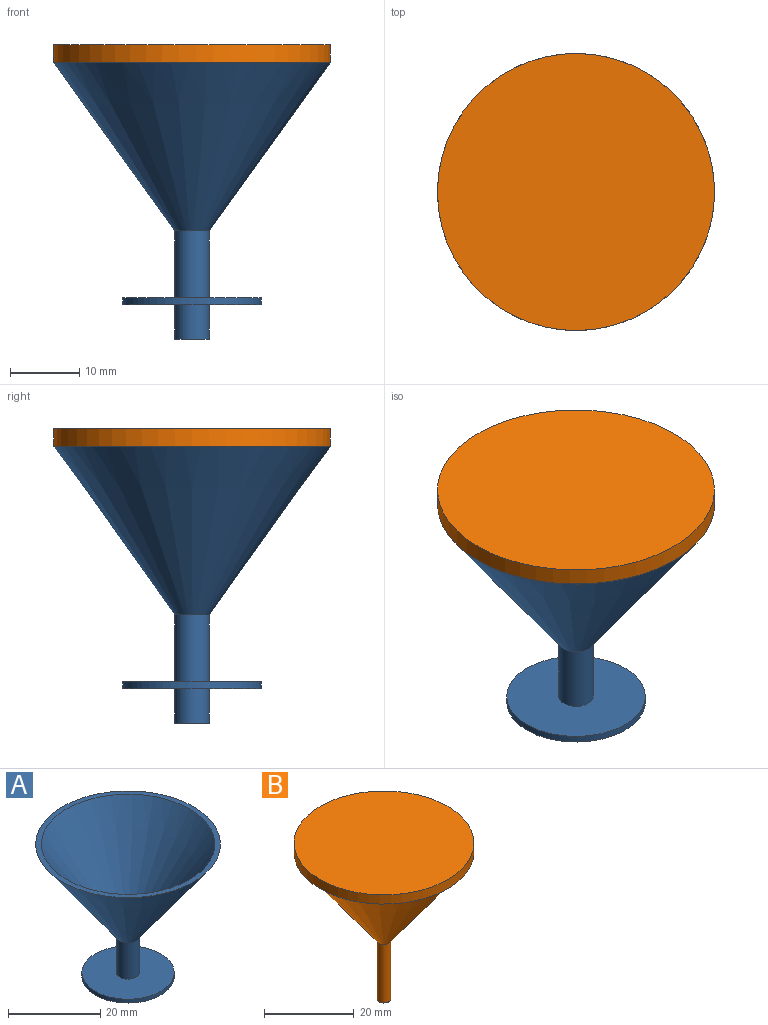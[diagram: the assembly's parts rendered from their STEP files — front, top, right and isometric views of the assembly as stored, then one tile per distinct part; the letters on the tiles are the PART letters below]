
ASSEMBLY  parts=2 mates=1
PART A: 10 faces, bbox 40x40x40 mm
  f0: cone r=18.77mm half-angle=35.7deg, axis (0,0,1), area 1885.1mm2, adj f1,f9
  f1: plane 40x40mm, normal (0,0,1), area 150mm2, adj f0,f2
  f2: cone r=20mm half-angle=35.7deg, axis (0,0,1), area 2120.6mm2, adj f1,f3
  f3: cylinder r=2.5mm len=9.63mm, axis (0,0,1), area 151.3mm2, adj f2,f4
  f4: plane 20x20mm, normal (0,0,1), area 294.5mm2, adj f3,f5
  f5: cylinder r=10mm len=20mm, axis (0,0,1), area 62.8mm2, adj f4,f6
  f6: plane 20x20mm, normal (0,0,-1), area 294.5mm2, adj f5,f7
  f7: cylinder r=2.5mm len=5mm, axis (0,0,1), area 78.5mm2, adj f6,f8
  f8: plane 5x5mm, normal (0,0,-1), area 12.6mm2, adj f7,f9
  f9: cylinder r=1.5mm len=15.96mm, axis (0,0,1), area 150.4mm2, adj f0,f8
PART B: 6 faces, bbox 40x40x42.5 mm
  f0: cylinder r=1.5mm len=15.96mm, axis (0,0,-1), area 150.4mm2, adj f1,f5
  f1: sphere r=1.5mm, area 14.1mm2, adj f0
  f2: plane 40x40mm, normal (0,0,1), area 1256.6mm2, adj f3
  f3: cylinder r=20mm len=40mm, axis (0,0,-1), area 314.2mm2, adj f2,f4
  f4: plane 40x40mm, normal (0,0,-1), area 122.5mm2, adj f3,f5
  f5: cone r=19mm half-angle=36deg, axis (0,0,1), area 1915.3mm2, adj f0,f4
PLACE A at identity
PLACE B at identity
MATE slider B.f0 <-> A.f0  axis (0,0,-1) through (0,0,0)mm
